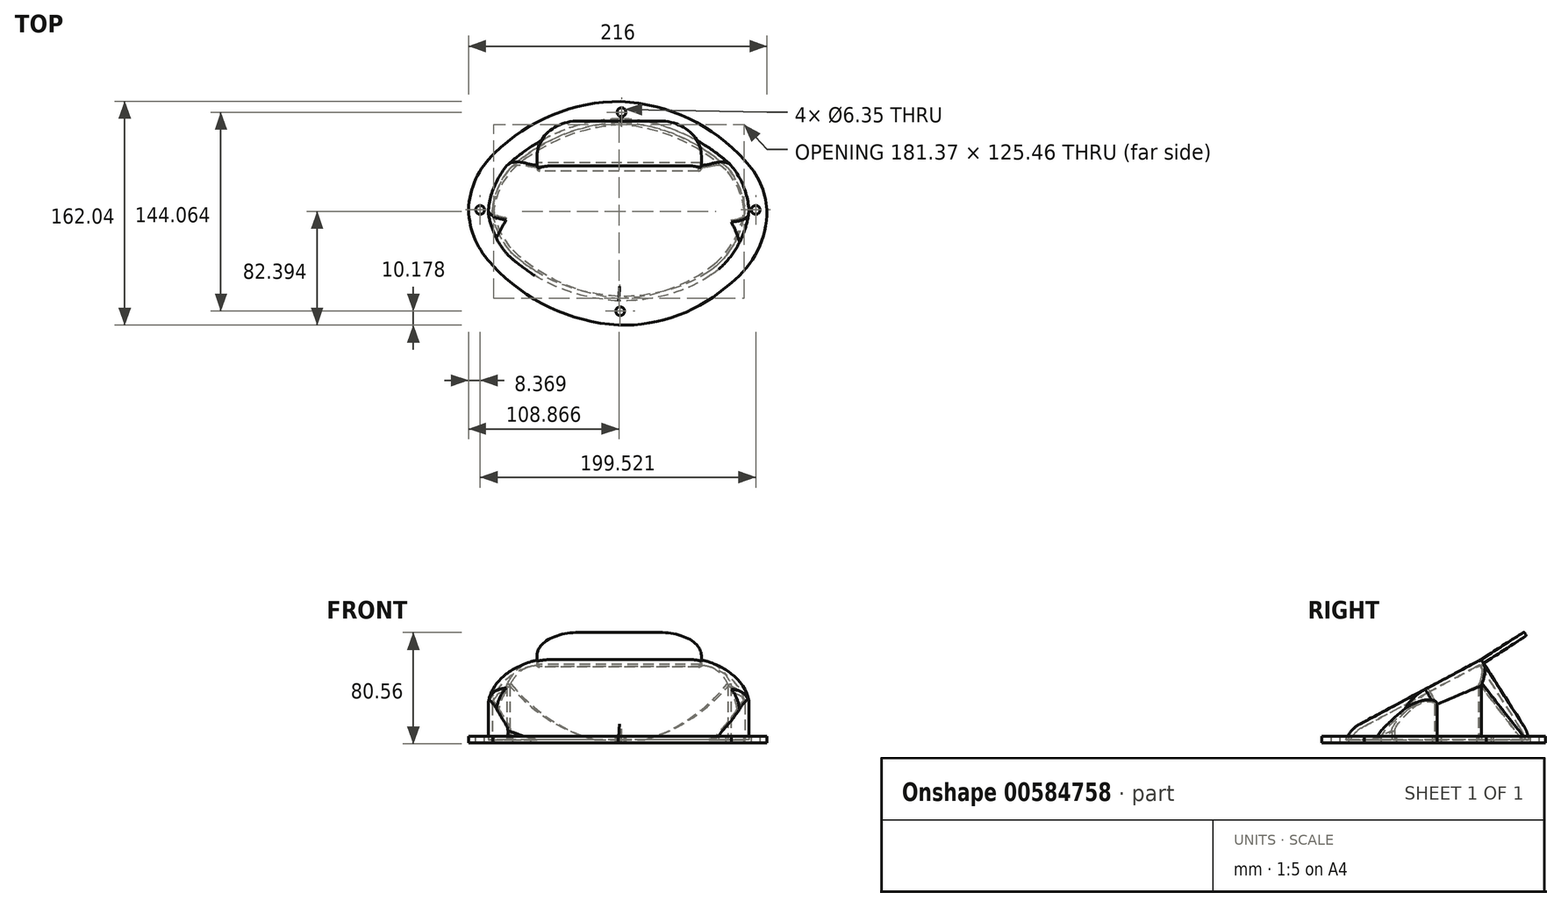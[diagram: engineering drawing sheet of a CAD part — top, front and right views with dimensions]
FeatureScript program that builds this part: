
annotation { "Feature Type Name" : "Feature", "Feature Type Description" : "" }
export const myFeature = defineFeature(function(context is Context, id is Id, definition is map)
    precondition{}
    {
        {
            var Q0;
            Q0=qCreatedBy(makeId("Right.planeOp"),FACE);
            var sketch = newSketch(context, id + "F0", { "sketchPlane" : qUnion([Q0])});
            skLineSegment(sketch, "E0", {"start": v(63.9, 0) * mm, "end": v(63.9, 71.69) * mm, "construction": true});
            skLineSegment(sketch, "E1", {"start": v(63.9, 0) * mm, "end": v(30.86, 0) * mm, "construction": true});
            skLineSegment(sketch, "E2", {"start": v(30.86, 0) * mm, "end": v(30.86, 51.54) * mm, "construction": true});
            skLineSegment(sketch, "E3", {"start": v(30.86, 51.54) * mm, "end": v(63.9, 0) * mm, "construction": true});
            skLineSegment(sketch, "E4", {"start": v(30.86, 51.54) * mm, "end": v(63.9, 0) * mm});
            skLineSegment(sketch, "E5", {"start": v(-65.97, 0) * mm, "end": v(30.86, 51.54) * mm});
            skLineSegment(sketch, "E6", {"start": v(-65.97, -2.5) * mm, "end": v(-65.97, 0) * mm});
            skLineSegment(sketch, "E7", {"start": v(63.9, 0) * mm, "end": v(63.9, -2.5) * mm});
            skLineSegment(sketch, "E8", {"start": v(-65.97, -2.5) * mm, "end": v(63.9, -2.5) * mm});
            skSolve(sketch);
        }
        {
            var Q0;
            Q0 = qSketchRegion(id + "F0", true);
            extrude(context, id + "F1", {"entities" : qUnion([Q0]), "depth" : 93 * mm, "offsetDistance" : 25 * mm, "hasSecondDirection" : true, "secondDirectionOppositeDirection" : true, "secondDirectionDepth" : 92 * mm});
        }
        {
            var Q0;
            Q0=qCreatedBy(makeId("Top.planeOp"),FACE);
            var sketch = newSketch(context, id + "F2", { "sketchPlane" : qUnion([Q0])});
            skArc(sketch, "E9.0", {"start": v(91.64, 0) * mm, "mid": v(87.83, 16.02) * mm, "end": v(79.48, 30.22) * mm});
            skArc(sketch, "E9.1", {"start": v(70.74, -40.73) * mm, "mid": v(85, -22.32) * mm, "end": v(91.64, 0) * mm});
            skArc(sketch, "E9.2", {"start": v(79.48, 30.22) * mm, "mid": v(43.79, 53.49) * mm, "end": v(2.4, 63.62) * mm});
            skArc(sketch, "E9.3", {"start": v(0.06, -64.73) * mm, "mid": v(37.44, -58.75) * mm, "end": v(70.74, -40.73) * mm});
            skArc(sketch, "E9.4", {"start": v(-78.42, 30) * mm, "mid": v(-41, 54) * mm, "end": v(2.4, 63.62) * mm});
            skArc(sketch, "E9.5", {"start": v(-91.11, -1.64) * mm, "mid": v(-87.26, 15.18) * mm, "end": v(-78.42, 30) * mm});
            skArc(sketch, "E9.6", {"start": v(-91.11, -1.64) * mm, "mid": v(-86.53, -17.12) * mm, "end": v(-77.68, -30.62) * mm});
            skArc(sketch, "E9.7", {"start": v(-77.68, -30.62) * mm, "mid": v(-41.63, -54.1) * mm, "end": v(0.06, -64.73) * mm});
            skArc(sketch, "E10.0", {"start": v(106.35, 56.84) * mm, "mid": v(123.67, 30.47) * mm, "end": v(131.2, -0.16) * mm});
            skArc(sketch, "E10.1", {"start": v(2.96, 101.46) * mm, "mid": v(58.6, 88.27) * mm, "end": v(106.35, 56.84) * mm});
            skArc(sketch, "E10.2", {"start": v(131.2, -0.16) * mm, "mid": v(120.02, -38.8) * mm, "end": v(94.65, -70.01) * mm});
            skArc(sketch, "E10.3", {"start": v(-84.6, 73.22) * mm, "mid": v(-42.83, 93.58) * mm, "end": v(2.96, 101.46) * mm});
            skArc(sketch, "E10.4", {"start": v(94.65, -70.01) * mm, "mid": v(49.3, -95.27) * mm, "end": v(-1.93, -103.64) * mm});
            skArc(sketch, "E10.5", {"start": v(-1.93, -103.64) * mm, "mid": v(-57.1, -89.25) * mm, "end": v(-104.4, -57.38) * mm});
            skArc(sketch, "E10.6", {"start": v(-104.4, -57.38) * mm, "mid": v(-122.25, -30.97) * mm, "end": v(-130.16, -0.09) * mm});
            skArc(sketch, "E10.7", {"start": v(-130.16, -0.09) * mm, "mid": v(-116.38, 42.16) * mm, "end": v(-84.6, 73.22) * mm});
            skSolve(sketch);
        }
        {
            var Q0;
            Q0 = qSketchRegion(id + "F2", true);
            extrude(context, id + "F3", {"entities" : qUnion([Q0]), "operationType" : NewBodyOperationType.REMOVE, "depth" : 100 * mm, "offsetDistance" : 25 * mm, "hasSecondDirection" : true, "secondDirectionOppositeDirection" : true, "secondDirectionDepth" : 25 * mm});
        }
        {
            var Q0;
            Q0=makeQuery(id+"F3.boolean.opBoolean","INTERSECT",EDGE,{"derivedFrom":[makeQuery(id+"F1.opExtrude","SWEPT_FACE",FACE,{"disambiguationData":[OSD([sQuery(id+"F0.wireOp",EDGE,"E4")])]}),makeQuery(id+"F3.opExtrude","SWEPT_FACE",FACE,{"disambiguationData":[OSD([sQuery(id+"F2.wireOp",EDGE,"E9.2")])]})]});
            var Q1;
            Q1=makeQuery(id+"F3.boolean.opBoolean","INTERSECT",EDGE,{"derivedFrom":[makeQuery(id+"F1.opExtrude","SWEPT_FACE",FACE,{"disambiguationData":[OSD([sQuery(id+"F0.wireOp",EDGE,"E4")])]}),makeQuery(id+"F3.opExtrude","SWEPT_FACE",FACE,{"disambiguationData":[OSD([sQuery(id+"F2.wireOp",EDGE,"E9.4")])]})]});
            fillet(context, id + "F4", {"entities" : qUnion([Q0, Q1]), "radius" : 20 * mm, "tangentPropagation" : true, "allowEdgeOverflow" : false});
        }
        {
            var Q0;
            Q0=makeQuery(id+"F3.boolean.opBoolean","INTERSECT",EDGE,{"derivedFrom":[makeQuery(id+"F1.opExtrude","SWEPT_FACE",FACE,{"disambiguationData":[OSD([sQuery(id+"F0.wireOp",EDGE,"E5")])]}),makeQuery(id+"F3.opExtrude","SWEPT_FACE",FACE,{"disambiguationData":[OSD([sQuery(id+"F2.wireOp",EDGE,"E9.3")])]})]});
            var Q1;
            Q1=makeQuery(id+"F3.boolean.opBoolean","INTERSECT",EDGE,{"derivedFrom":[makeQuery(id+"F1.opExtrude","SWEPT_FACE",FACE,{"disambiguationData":[OSD([sQuery(id+"F0.wireOp",EDGE,"E5")])]}),makeQuery(id+"F3.opExtrude","SWEPT_FACE",FACE,{"disambiguationData":[OSD([sQuery(id+"F2.wireOp",EDGE,"E9.7")])]})]});
            fillet(context, id + "F5", {"entities" : qUnion([Q0, Q1]), "radius" : 20 * mm, "tangentPropagation" : true, "allowEdgeOverflow" : false});
        }
        {
            var Q0;
            Q0=makeQuery(id+"F5.opFillet","BLEND_EDGE",EDGE,{"blendedFrom":[makeQuery(id+"F3.boolean.opBoolean","INTERSECT",EDGE,{"derivedFrom":[makeQuery(id+"F1.opExtrude","SWEPT_FACE",FACE,{"disambiguationData":[OSD([sQuery(id+"F0.wireOp",EDGE,"E5")])]}),makeQuery(id+"F3.opExtrude","SWEPT_FACE",FACE,{"disambiguationData":[OSD([sQuery(id+"F2.wireOp",EDGE,"E9.3")])]})]}),makeQuery(id+"F3.boolean.opBoolean","COPY",FACE,{"derivedFrom":makeQuery(id+"F3.opExtrude","SWEPT_FACE",FACE,{"disambiguationData":[OSD([sQuery(id+"F2.wireOp",EDGE,"E9.0")])]})})],"blendedInto":[makeQuery(id+"F3.boolean.opBoolean","COPY",FACE,{"derivedFrom":makeQuery(id+"F3.opExtrude","SWEPT_FACE",FACE,{"disambiguationData":[OSD([sQuery(id+"F2.wireOp",EDGE,"E9.0")])]})})]});
            var Q1;
            Q1=makeQuery(id+"F3.boolean.opBoolean","INTERSECT",EDGE,{"derivedFrom":[makeQuery(id+"F1.opExtrude","SWEPT_FACE",FACE,{"disambiguationData":[OSD([sQuery(id+"F0.wireOp",EDGE,"E5")])]}),makeQuery(id+"F3.opExtrude","SWEPT_FACE",FACE,{"disambiguationData":[OSD([sQuery(id+"F2.wireOp",EDGE,"E9.5")])]})]});
            fillet(context, id + "F6", {"entities" : qUnion([Q0, Q1]), "radius" : 10 * mm, "tangentPropagation" : true, "allowEdgeOverflow" : false});
        }
        {
            var Q0;
            Q0=makeQuery(id+"F1.boolean.opBoolean","SPLIT",FACE,{"disambiguationData":[TD([makeQuery(id+"F9.opExtrude","SWEPT_FACE",FACE,{"disambiguationData":[OSD([sQuery(id+"F8.wireOp",EDGE,"E19.0")])]})])],"derivedFrom":makeQuery(id+"F1.opExtrude","SWEPT_FACE",FACE,{"disambiguationData":[OSD([sQuery(id+"F0.wireOp",EDGE,"E8")])]})});
            shell(context, id + "F7", {"entities" : qUnion([Q0]), "thickness" : 3 * mm, "oppositeDirection" : true});
        }
        {
            var Q0;
            Q0=qCreatedBy(makeId("Top.planeOp"),FACE);
            var sketch = newSketch(context, id + "F8", { "sketchPlane" : qUnion([Q0])});
            skArc(sketch, "E11", {"start": v(91.73, 35.75) * mm, "mid": v(51.05, 66.1) * mm, "end": v(1.84, 78.53) * mm});
            skArc(sketch, "E12", {"start": v(107.66, 0) * mm, "mid": v(102.78, 19.25) * mm, "end": v(91.73, 35.75) * mm});
            skArc(sketch, "E13.MirrorCS", {"start": v(-89.66, 40.95) * mm, "mid": v(-47.63, 68.8) * mm, "end": v(1.84, 78.53) * mm});
            skArc(sketch, "E14.MirrorCS", {"start": v(-108.34, 0) * mm, "mid": v(-103.1, 22.35) * mm, "end": v(-89.66, 40.95) * mm});
            skArc(sketch, "E15.MirrorCS", {"start": v(-108.34, 0) * mm, "mid": v(-103.45, -21.78) * mm, "end": v(-90.75, -40.14) * mm});
            skArc(sketch, "E16", {"start": v(81.74, -52.74) * mm, "mid": v(100.87, -29.4) * mm, "end": v(107.66, 0) * mm});
            skArc(sketch, "E17", {"start": v(0, -83.47) * mm, "mid": v(43.88, -76.1) * mm, "end": v(81.74, -52.74) * mm});
            skArc(sketch, "E18", {"start": v(-90.75, -40.14) * mm, "mid": v(-49.57, -70.59) * mm, "end": v(0, -83.47) * mm});
            skArc(sketch, "E19.0", {"start": v(-90.16, 0) * mm, "mid": v(-81.43, 22.92) * mm, "end": v(-63.38, 39.52) * mm});
            skArc(sketch, "E19.1", {"start": v(-90.16, 0) * mm, "mid": v(-85.47, -15.68) * mm, "end": v(-76.26, -29.2) * mm});
            skArc(sketch, "E19.2", {"start": v(-63.38, 39.52) * mm, "mid": v(-32.07, 55.23) * mm, "end": v(2.37, 61.61) * mm});
            skArc(sketch, "E19.3", {"start": v(-76.26, -29.2) * mm, "mid": v(-41, -52.85) * mm, "end": v(0, -63.84) * mm});
            skArc(sketch, "E19.4", {"start": v(78.05, 28.81) * mm, "mid": v(43, 51.65) * mm, "end": v(2.37, 61.61) * mm});
            skArc(sketch, "E19.5", {"start": v(91.21, 0) * mm, "mid": v(86.82, 15.4) * mm, "end": v(78.05, 28.81) * mm});
            skArc(sketch, "E19.6", {"start": v(69.48, -39.18) * mm, "mid": v(84.06, -21.65) * mm, "end": v(91.21, 0) * mm});
            skArc(sketch, "E19.7", {"start": v(0, -63.84) * mm, "mid": v(36.85, -57.46) * mm, "end": v(69.48, -39.18) * mm});
            skCircle(sketch, "E20", {"center": v(2.4, 70.73) * mm, "radius": 3.17 * mm});
            skCircle(sketch, "E21", {"center": v(99.55, 0) * mm, "radius": 3.17 * mm});
            skCircle(sketch, "E22", {"center": v(1.37, -73.33) * mm, "radius": 3.17 * mm});
            skCircle(sketch, "E23", {"center": v(-99.97, 0) * mm, "radius": 3.17 * mm});
            skSolve(sketch);
        }
        {
            var Q0;
            Q0=qSketchRegion(id+"F8",true);
            extrude(context, id + "F9", {"entities" : qUnion([Q0]), "oppositeDirection" : true, "depth" : 5 * mm, "offsetDistance" : 25 * mm});
        }
        {
            var Q0;
            Q0=makeQuery(id+"F1.opExtrude","SWEPT_FACE",FACE,{"disambiguationData":[OSD([sQuery(id+"F0.wireOp",EDGE,"E4")])]});
            var sketch = newSketch(context, id + "F10", { "sketchPlane" : qUnion([Q0])});
            skLineSegment(sketch, "E24.bottom", {"start": v(-60.14, 29.5) * mm, "end": v(58.82, 29.5) * mm});
            skLineSegment(sketch, "E24.top", {"start": v(-60.14, 26.3) * mm, "end": v(58.82, 26.3) * mm});
            skLineSegment(sketch, "E24.left", {"start": v(-60.14, 29.5) * mm, "end": v(-60.14, 26.3) * mm});
            skLineSegment(sketch, "E24.right", {"start": v(58.82, 29.5) * mm, "end": v(58.82, 26.3) * mm});
            skSolve(sketch);
        }
        {
            var Q0;
            Q0 = qSketchRegion(id + "F10", true);
            extrude(context, id + "F11", {"entities" : qUnion([Q0]), "operationType" : NewBodyOperationType.ADD, "depth" : 37 * mm, "offsetDistance" : 25 * mm, "hasSecondDirection" : true, "secondDirectionOppositeDirection" : true, "secondDirectionDepth" : 6 * mm});
        }
        {
            var Q0;
            Q0=makeQuery(id+"F11.opExtrude","CAP_EDGE",EDGE,{"disambiguationData":[OSD([sQuery(id+"F10.wireOp",EDGE,"E24.left")])],"isStart":false});
            var Q1;
            Q1=makeQuery(id+"F11.opExtrude","CAP_EDGE",EDGE,{"disambiguationData":[OSD([sQuery(id+"F10.wireOp",EDGE,"E24.right")])],"isStart":false});
            fillet(context, id + "F12", {"entities" : qUnion([Q0, Q1]), "radius" : 30 * mm, "tangentPropagation" : true, "allowEdgeOverflow" : false});
        }
        {
            var Q0;
            Q0=makeQuery(id+"F1.opExtrude","SWEPT_FACE",FACE,{"disambiguationData":[OSD([sQuery(id+"F0.wireOp",EDGE,"E4")])]});
            var sketch = newSketch(context, id + "F13", { "sketchPlane" : qUnion([Q0])});
            skLineSegment(sketch, "E25.bottom", {"start": v(-60.14, 26.3) * mm, "end": v(58.82, 26.3) * mm});
            skLineSegment(sketch, "E25.top", {"start": v(-60.14, 25.3) * mm, "end": v(58.82, 25.3) * mm});
            skLineSegment(sketch, "E25.left", {"start": v(-60.14, 26.3) * mm, "end": v(-60.14, 25.3) * mm});
            skLineSegment(sketch, "E25.right", {"start": v(58.82, 26.3) * mm, "end": v(58.82, 25.3) * mm});
            skSolve(sketch);
        }
        {
            var Q0;
            Q0 = qSketchRegion(id + "F13", true);
            extrude(context, id + "F14", {"entities" : qUnion([Q0]), "operationType" : NewBodyOperationType.REMOVE, "oppositeDirection" : true, "depth" : 3 * mm, "offsetDistance" : 25 * mm});
        }
        {
            var Q0;
            Q0=makeQuery(id+"F11.opExtrude","CAP_EDGE",EDGE,{"disambiguationData":[OSD([sQuery(id+"F10.wireOp",EDGE,"E24.top")])],"isStart":true});
            fillet(context, id + "F15", {"entities" : qUnion([Q0]), "radius" : 5 * mm, "tangentPropagation" : true, "allowEdgeOverflow" : false});
        }
        {
            var Q0;
            {var subQ0=sQuery(id+"F10.wireOp",EDGE,"E24.left");var subQ1=sQuery(id+"F10.wireOp",EDGE,"E24.top");Q0=makeQuery(id+"F15.opFillet","BLEND_EDGE",EDGE,{"blendedFrom":[makeQuery(id+"F11.opExtrude","CAP_EDGE",EDGE,{"disambiguationData":[OSD([subQ1])],"isStart":true}),makeQuery(id+"F11.boolean.opBoolean","SPLIT",FACE,{"disambiguationData":[TD([makeQuery(id+"F7.opShell","OFFSET_FACE",FACE,{"disambiguationData":[OSD([sQuery(id+"F0.wireOp",EDGE,"E4")])]})])],"derivedFrom":makeQuery(id+"F11.opExtrude","SWEPT_FACE",FACE,{"disambiguationData":[OSD([subQ0])]})})],"blendedInto":[makeQuery(id+"F11.boolean.opBoolean","SPLIT",FACE,{"disambiguationData":[TD([makeQuery(id+"F7.opShell","OFFSET_FACE",FACE,{"disambiguationData":[OSD([sQuery(id+"F0.wireOp",EDGE,"E4")])]})])],"derivedFrom":makeQuery(id+"F11.opExtrude","SWEPT_FACE",FACE,{"disambiguationData":[OSD([subQ0])]})})]});}
            var Q1;
            {var subQ0=sQuery(id+"F10.wireOp",EDGE,"E24.right");var subQ1=sQuery(id+"F10.wireOp",EDGE,"E24.top");Q1=makeQuery(id+"F15.opFillet","BLEND_EDGE",EDGE,{"blendedFrom":[makeQuery(id+"F11.opExtrude","CAP_EDGE",EDGE,{"disambiguationData":[OSD([subQ1])],"isStart":true}),makeQuery(id+"F11.boolean.opBoolean","SPLIT",FACE,{"disambiguationData":[TD([makeQuery(id+"F7.opShell","OFFSET_FACE",FACE,{"disambiguationData":[OSD([sQuery(id+"F0.wireOp",EDGE,"E4")])]})])],"derivedFrom":makeQuery(id+"F11.opExtrude","SWEPT_FACE",FACE,{"disambiguationData":[OSD([subQ0])]})})],"blendedInto":[makeQuery(id+"F11.boolean.opBoolean","SPLIT",FACE,{"disambiguationData":[TD([makeQuery(id+"F7.opShell","OFFSET_FACE",FACE,{"disambiguationData":[OSD([sQuery(id+"F0.wireOp",EDGE,"E4")])]})])],"derivedFrom":makeQuery(id+"F11.opExtrude","SWEPT_FACE",FACE,{"disambiguationData":[OSD([subQ0])]})})]});}
            fillet(context, id + "F16", {"entities" : qUnion([Q0, Q1]), "radius" : 5 * mm, "tangentPropagation" : true, "allowEdgeOverflow" : false});
        }
        {
            var Q0;
            Q0=makeQuery(id+"F11.opExtrude","SWEPT_EDGE",EDGE,{"disambiguationData":[OSD([sQuery(id+"F10.wireOp",EDGE,"E24.bottom"),sQuery(id+"F10.wireOp",EDGE,"E24.left")])]});
            var Q1;
            Q1=makeQuery(id+"F11.opExtrude","CAP_EDGE",EDGE,{"disambiguationData":[OSD([sQuery(id+"F10.wireOp",EDGE,"E24.top")])],"isStart":false});
            fillet(context, id + "F17", {"entities" : qUnion([Q0, Q1]), "radius" : 1 * mm, "tangentPropagation" : true, "allowEdgeOverflow" : false});
        }
    });
